# Revit family: KDW010037
name_source: partatom
category: Plumbing Fixtures
revit_build: Autodesk Revit 2015 (Build: 20140606_1530(x64)
units: mm (PartAtom-declared; Revit-internal decimal feet)

## types (1)
- KDW010037
    Accessory = Yes
    BIMobject category = Bath & Spas
    Brand url = http://www.kaldewei.com
    Chrome = Chrome
    Color = https://www.kaldewei.co.uk
    ColourOptions = https://www.kaldewei.co.uk
    ConnectingDimensions = EN 232
    Design country = Germany
    DrainSize = 52 mm
    Durability = https://www.kaldewei.de
    Edition number = 1
    Features = https://www.kaldewei.co.uk
    Finish = https://www.kaldewei.co.uk
    Finition = Kaldewei
    HasGrabHandles = https://www.kaldewei.co.uk
    IFC Classification = Furnishing Element
    IfcExportAs = BATH
    IfcExportType = IfcSanitaryTerminalType
    IntegralAccessories = https://www.kaldewei.co.uk
    Manufacturer = Kaldewei
    Manufacturer country = Germany
    ManufacturerCountry = GERMANY
    ManufacturerName = KALDEWEI
    ManufacturerURL = https://www.kaldewei.com
    Material = steel enamel
    Material main = Steel
    Material secondary = Enamel
    Model = PURO DUO
    NBS Reference Code = 35-06-08
    NBS Reference Description = Baths
    Name = PURO DUO
    Nominal height = 800 cm
    Nominal width = 1800 cm
    NominalDepth = 420
    NominalLength = 1800
    ObjectName = PURO DUO 800x1800x420
    ObjectNorm = EN 14516EU DECLARATION OF PERFORMANCE(https://www.kaldewei.de
    ObjectPicture = https://www.kaldewei.co.uk
    ObjectURL = https://www.kaldewei.co.uk
    Polantis code = KDW010037
    Product Guid = 7fdc2ee6-a281-4064-865d-a8ffbb27874e
    Product SKU = 664
    Product certification = https://www.kaldewei.co.uk
    Product data url = https://bimobject.com
    Product family = PURO
    Product group = Bathtub
    Product url = https://www.kaldewei.co.uk
    ProductInformation = Model No.664: One of the basic principles of modern architecture and interior design is the reduction of all elements to the essentials. The clear and purist design of the PURO DUO bath follows this approach and is the logical continuation of the successful PURO series. It fulfils the desire for high-quality and timeless design for bathing for two.The inside of the PURO DUO is especially long to offer exceptional bathing comfort.
    QR code = http://bimobject.com
    Revision = 1
    SerialNumber = 664
    Shape = Rectangular baths
    Size = 800x1800x420
    SupportFrame = https://www.kaldewei.co.uk
    Sustainability = https://kaldewei-fa.secure.footprint.net
    Technical description = https://www.kaldewei.co.uk
    TechnicalDataURL = https://kaldewei.typo-live.web-factory.de
    Type Comments = PURO DUO 664 800x1800x420
    UNSPSC Code = 30181501
    UNSPSCCode = 30181500
    UNSPSCNames = Sanitary ware
    URL = https://www.kaldewei.co.uk
    Uniclass 1.4 Code = L7211
    Uniclass 1.4 Description = Baths
    Uniclass 2.0 Code = PR-35-06-08
    Uniclass 2.0 Description = Baths
    Uniclass 2015 = Pr_40_20_06_08
    Version = 5
    VolumeToOverflowMaximum = 165
    WarrantyDurationParts = 30
    WarrantyDurationUnit = Year
    WarrantyStartDate = https://www.kaldewei.co.uk
    WaterSupplyOverflowAndWasteHolesOverflow = 52 mm
    WaterSupplyOverflowAndWasteHolesWaste = 52 mm
    Weight = 54
    Weight Net (Kg) = 54

## geometry (parser evidence)
native form markers: Sweep x10
no freeform markers — native parametric forms only
